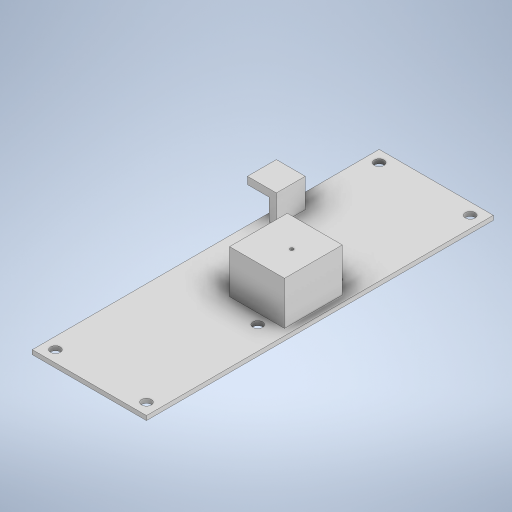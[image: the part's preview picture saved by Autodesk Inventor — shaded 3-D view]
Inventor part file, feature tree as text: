
AUTODESK INVENTOR PART (.ipt)
format: ipt  version: 2023 (Build 270158000, 158)  size: 302,080 bytes
history: native  units: mm
features: extrude x8, sketch x8
ambient origin geometry x8: Origin, YZ Plane, XZ Plane, XY Plane, X Axis, Y Axis, Z Axis, Center Point
bodies: Body1 (feature_tree)
feature tree (16):
  extrude  "Extrusion33"  Depth=240.0mm
  extrude  "Extrusion34"  Depth=38.0mm
  extrude  "Extrusion35"  Depth=30.0mm TaperAngle=0.0deg
  extrude  "Extrusion40"  Depth=30.0mm
  extrude  "Extrusion41"  Depth=20.0mm
  extrude  "Extrusion46"  Depth=20.0mm
  extrude  "Extrusion47"  Depth=5.0mm TaperAngle=0.0deg
  extrude  "Extrusion51"  Depth=10.0mm
  sketch  "Sketch44"  dims[d138=79.0mm d139=240.0mm]
  sketch  "Sketch45"  dims[d140=3.0mm d141=0.0mm d142=38.0mm]
  sketch  "Sketch47"  dims[d143=40.0mm d144=30.0mm d145=0.0mm]
  sketch  "Sketch60"  dims[d146=36.0mm d147=30.0mm d148=-2.617994mm]
  sketch  "Sketch61"  dims[d164=5.0mm d165=20.0mm]
  sketch  "Sketch68"  dims[d166=20.0mm d167=0.0mm d168=20.0mm]
  sketch  "Sketch69"  dims[d169=20.0mm d170=5.0mm d171=0.0mm]
  sketch  "Sketch74"  dims[d192=6.7mm d193=6.7mm d194=6.7mm d195=6.7mm d196=10.0mm d197=0.0mm d198=6.7mm d199=6.7mm d200=10.0mm d201=0.0mm d210=2.3mm d211=10.0mm d212=0.0mm d49=0.5mm d50=0.872665mm d51=0.5mm d52=0.872665mm d130=0.5mm d131=0.872665mm d132=0.5mm d133=0.872665mm d156=0.5mm d157=0.872665mm d158=0.5mm d159=0.872665mm d173=0.5mm d174=0.872665mm d175=0.5mm d176=0.872665mm]
